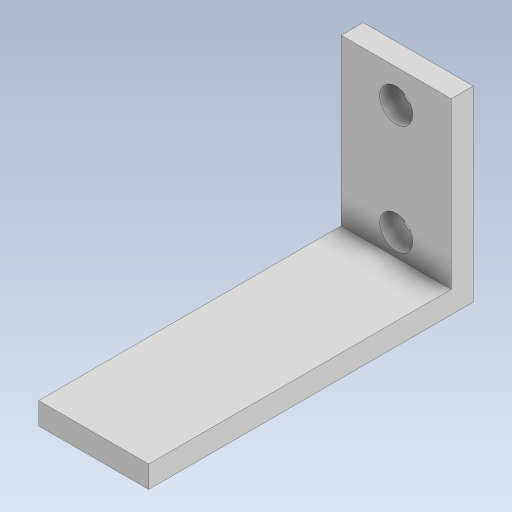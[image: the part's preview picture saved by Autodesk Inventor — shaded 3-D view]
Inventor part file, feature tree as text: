
AUTODESK INVENTOR PART (.ipt)
format: ipt  version: 2023.5 (Build 275446000, 446)  size: 115,712 bytes
history: native  units: in
note: dims shown in document units (in); Inventor stores cm internally (conversion verified against a paired STEP export)
features: extrude x3, sketch x3
ambient origin geometry x8: Origin, YZ Plane, XZ Plane, XY Plane, X Axis, Y Axis, Z Axis, Center Point
bodies: Solid1 (feature_tree)
feature tree (6):
  extrude  "Extrusion1"  Depth=1.1614in
  extrude  "Extrusion2"  Depth=0.0787in
  extrude  "Extrusion3"  Depth=0.5906in
  sketch  "Sketch1"  dims[d0=0.3937in d1=1.1614in]
  sketch  "Sketch2"  dims[d2=0.0787in d3=0.0in d4=0.0787in]
  sketch  "Sketch3"  dims[d5=0.5906in d6=0.0in d7=0.1181in d8=0.1181in d9=0.0787in d10=0.3937in d11=0.5906in d12=0.0in]
